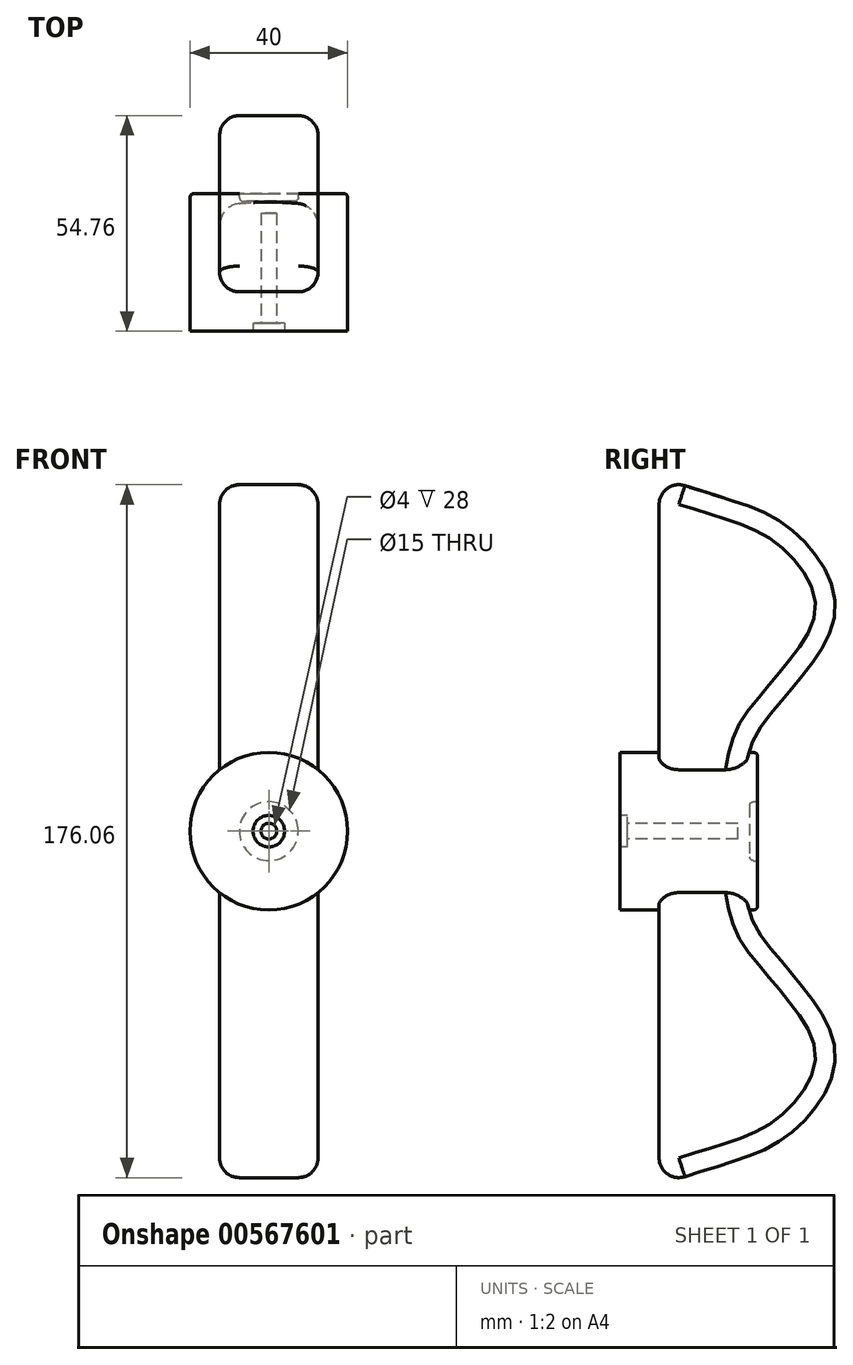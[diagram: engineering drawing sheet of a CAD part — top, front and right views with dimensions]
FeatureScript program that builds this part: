
annotation { "Feature Type Name" : "Feature", "Feature Type Description" : "" }
export const myFeature = defineFeature(function(context is Context, id is Id, definition is map)
    precondition{}
    {
        {
            var Q0;
            Q0=qCreatedBy(makeId("Front.planeOp"),FACE);
            var sketch = newSketch(context, id + "F0", { "sketchPlane" : qUnion([Q0])});
            skCircle(sketch, "E0", {"center": v(0, 0) * mm, "radius": 20 * mm});
            skSolve(sketch);
        }
        {
            var Q0;
            Q0 = qSketchRegion(id + "F0", true);
            extrude(context, id + "F1", {"entities" : qUnion([Q0]), "depth" : 10 * mm, "offsetDistance" : 25 * mm});
        }
        {
            var Q0;
            Q0=qCreatedBy(makeId("Right.planeOp"),FACE);
            var sketch = newSketch(context, id + "F2", { "sketchPlane" : qUnion([Q0])});
            skLineSegment(sketch, "E1", {"start": v(0, 90) * mm, "end": v(0, -90) * mm});
            skLineSegment(sketch, "E2", {"start": v(0, 0) * mm, "end": v(20, 0) * mm});
            skFitSpline(sketch, "E3", {"points": [v(0, -90) * mm, v(30.9, -78.56) * mm, v(43.47, -63.7) * mm, v(42.5, -48.53) * mm, v(26.9, -28) * mm, v(20, 0) * mm], "startDerivative": vector(203.31, 71.49) * mm, "endDerivative": vector(-28.65, 263.02) * mm});
            skFitSpline(sketch, "E4.MirrorCS", {"points": [v(0, 90) * mm, v(30.9, 78.56) * mm, v(43.47, 63.7) * mm, v(42.5, 48.53) * mm, v(26.9, 28) * mm, v(20, 0) * mm], "startDerivative": vector(203.31, -71.49) * mm, "endDerivative": vector(-28.65, -263.02) * mm});
            skSolve(sketch);
        }
        {
            var Q0;
            {var subQ2=sQuery(id+"F2.wireOp",EDGE,"E2");Q0=makeQuery(id+"F2.imprint","IMPRINT",FACE,{"disambiguationData":[TD([[makeQuery(id+"F2.imprint","IMPRINT",EDGE,{"derivedFrom":subQ2}),-1.0]])]});}
            var Q1;
            {var subQ2=sQuery(id+"F2.wireOp",EDGE,"E2");Q1=makeQuery(id+"F2.imprint","IMPRINT",FACE,{"disambiguationData":[TD([[makeQuery(id+"F2.imprint","IMPRINT",EDGE,{"derivedFrom":subQ2}),1.0]])]});}
            extrude(context, id + "F3", {"entities" : qUnion([Q0, Q1]), "endBound" : BoundingType.SYMMETRIC, "depth" : 25 * mm, "offsetDistance" : 25 * mm});
        }
        {
            var Q0;
            Q0=makeQuery(id+"F3.opExtrude","CAP_EDGE",EDGE,{"disambiguationData":[OSD([sQuery(id+"F2.wireOp",EDGE,"E3")])],"isStart":true});
            var Q1;
            Q1=makeQuery(id+"F3.opExtrude","CAP_EDGE",EDGE,{"disambiguationData":[OSD([sQuery(id+"F2.wireOp",EDGE,"E4.MirrorCS")])],"isStart":true});
            var Q2;
            Q2=makeQuery(id+"F3.opExtrude","CAP_EDGE",EDGE,{"disambiguationData":[OSD([sQuery(id+"F2.wireOp",EDGE,"E4.MirrorCS")])],"isStart":false});
            var Q3;
            Q3=makeQuery(id+"F3.opExtrude","CAP_EDGE",EDGE,{"disambiguationData":[OSD([sQuery(id+"F2.wireOp",EDGE,"E3")])],"isStart":false});
            fillet(context, id + "F4", {"entities" : qUnion([Q0, Q1, Q2, Q3]), "radius" : 5 * mm, "tangentPropagation" : true, "allowEdgeOverflow" : false});
        }
        {
            var Q0;
            Q0=makeQuery(id+"F3.opExtrude","SWEPT_EDGE",EDGE,{"disambiguationData":[OSD([sQuery(id+"F2.wireOp",EDGE,"E1"),sQuery(id+"F2.wireOp",EDGE,"E3")])]});
            fillet(context, id + "F5", {"entities" : qUnion([Q0]), "radius" : 5 * mm, "tangentPropagation" : true, "allowEdgeOverflow" : false});
        }
        {
            var Q0;
            Q0=makeQuery(id+"F1.opExtrude","CAP_FACE",FACE,{"disambiguationData":[OSD([sQuery(id+"F0.wireOp",EDGE,"E0")])],"isStart":false});
            var sketch = newSketch(context, id + "F6", { "sketchPlane" : qUnion([Q0])});
            skCircle(sketch, "E5", {"center": v(0, 0) * mm, "radius": 2 * mm});
            skSolve(sketch);
        }
        {
            var Q0;
            Q0=makeQuery(id+"F1.opExtrude","CAP_FACE",FACE,{"disambiguationData":[OSD([sQuery(id+"F0.wireOp",EDGE,"E0")])],"isStart":true});
            extrude(context, id + "F7", {"entities" : qUnion([Q0]), "operationType" : NewBodyOperationType.ADD, "depth" : 25 * mm, "offsetDistance" : 25 * mm});
        }
        {
            var Q0;
            Q0=makeQuery(id+"F6.imprint","IMPRINT",FACE,{"disambiguationData":[TD([[makeQuery(id+"F6.imprint","IMPRINT",EDGE,{"derivedFrom":sQuery(id+"F6.wireOp",EDGE,"E5")}),1.0]])]});
            var sketch = newSketch(context, id + "F8", { "sketchPlane" : qUnion([Q0])});
            skCircle(sketch, "E6", {"center": v(0, 0) * mm, "radius": 4 * mm});
            skCircle(sketch, "E7", {"center": v(0, 0) * mm, "radius": 2 * mm});
            skSolve(sketch);
        }
        {
            var Q0;
            Q0=makeQuery(id+"F6.imprint","IMPRINT",FACE,{"disambiguationData":[TD([[makeQuery(id+"F6.imprint","IMPRINT",EDGE,{"derivedFrom":sQuery(id+"F6.wireOp",EDGE,"E5")}),1.0]])]});
            extrude(context, id + "F9", {"entities" : qUnion([Q0]), "operationType" : NewBodyOperationType.REMOVE, "oppositeDirection" : true, "depth" : 30 * mm, "offsetDistance" : 25 * mm});
        }
        {
            var Q0;
            Q0=makeQuery(id+"F8.imprint","IMPRINT",FACE,{"disambiguationData":[TD([[makeQuery(id+"F8.imprint","IMPRINT",EDGE,{"derivedFrom":sQuery(id+"F8.wireOp",EDGE,"E6")}),1.0]])]});
            extrude(context, id + "F10", {"entities" : qUnion([Q0]), "operationType" : NewBodyOperationType.REMOVE, "oppositeDirection" : true, "depth" : 2 * mm, "offsetDistance" : 25 * mm});
        }
        {
            var Q0;
            Q0=makeQuery(id+"F7.opExtrude","CAP_FACE",FACE,{"disambiguationData":[OSD([sQuery(id+"F0.wireOp",EDGE,"E0")])],"isStart":false});
            var sketch = newSketch(context, id + "F11", { "sketchPlane" : qUnion([Q0])});
            skCircle(sketch, "E8", {"center": v(0, 0) * mm, "radius": 7.5 * mm});
            skSolve(sketch);
        }
        {
            var Q0;
            Q0 = qSketchRegion(id + "F11", true);
            extrude(context, id + "F12", {"entities" : qUnion([Q0]), "operationType" : NewBodyOperationType.REMOVE, "oppositeDirection" : true, "depth" : 2 * mm, "offsetDistance" : 25 * mm});
        }
        {
            var Q0;
            Q0=makeQuery(id+"F12.boolean.opBoolean","COPY",EDGE,{"derivedFrom":makeQuery(id+"F12.opExtrude","CAP_EDGE",EDGE,{"disambiguationData":[OSD([sQuery(id+"F11.wireOp",EDGE,"E8")])],"isStart":true})});
            var Q1;
            Q1=makeQuery(id+"F12.boolean.opBoolean","COPY",FACE,{"derivedFrom":makeQuery(id+"F12.opExtrude","CAP_FACE",FACE,{"disambiguationData":[OSD([sQuery(id+"F11.wireOp",EDGE,"E8")])],"isStart":false})});
            var Q2;
            Q2=makeQuery(id+"F7.opExtrude","CAP_EDGE",EDGE,{"disambiguationData":[OSD([sQuery(id+"F0.wireOp",EDGE,"E0")])],"isStart":false});
            fillet(context, id + "F13", {"entities" : qUnion([Q0, Q1, Q2]), "radius" : 1 * mm, "tangentPropagation" : true, "allowEdgeOverflow" : false});
        }
    });
